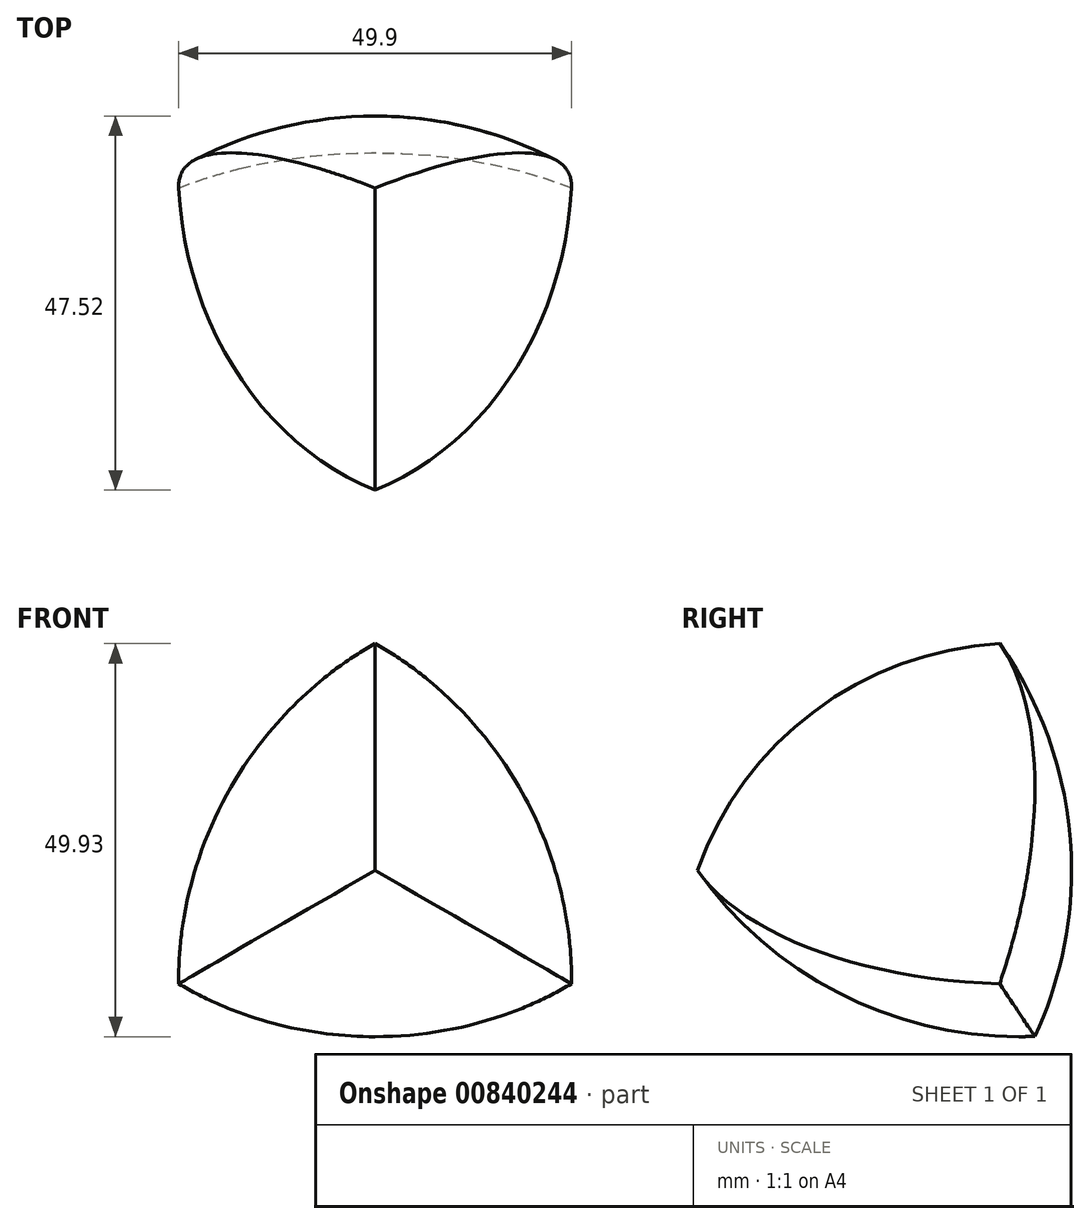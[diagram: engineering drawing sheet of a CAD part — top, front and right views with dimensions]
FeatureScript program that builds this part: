
annotation { "Feature Type Name" : "Feature", "Feature Type Description" : "" }
export const myFeature = defineFeature(function(context is Context, id is Id, definition is map)
    precondition{}
    {
        {
            var Q0;
            Q0=qCreatedBy(makeId("Front.planeOp"),FACE);
            var sketch = newSketch(context, id + "F0", { "sketchPlane" : qUnion([Q0])});
            skCircle(sketch, "E0", {"center": v(0, 0) * mm, "radius": 28.87 * mm, "construction": true});
            skCircle(sketch, "E1", {"center": v(0, 28.87) * mm, "radius": 50 * mm, "construction": true});
            skCircle(sketch, "E2", {"center": v(-25, -14.43) * mm, "radius": 50 * mm, "construction": true});
            skCircle(sketch, "E3", {"center": v(25, -14.43) * mm, "radius": 50 * mm, "construction": true});
            skSolve(sketch);
        }
        {
            var Q0;
            Q0=qCreatedBy(makeId("Front.planeOp"),FACE);
            var sketch = newSketch(context, id + "F1", { "sketchPlane" : qUnion([Q0])});
            skLineSegment(sketch, "E4", {"start": v(0, 0) * mm, "end": v(0, 85.02) * mm, "construction": true});
            skArc(sketch, "E5", {"start": v(0, -21.13) * mm, "mid": v(50, 28.87) * mm, "end": v(0, 78.87) * mm});
            skLineSegment(sketch, "E6", {"start": v(0, -21.13) * mm, "end": v(0, 78.87) * mm});
            skSolve(sketch);
        }
        {
            var Q0;
            Q0 = qSketchRegion(id + "F1", true);
            var Q1;
            Q1=sQuery(id+"F1.wireOp",EDGE,"E4");
            revolve(context, id + "F2", {"surfaceOperationType" : NewSurfaceOperationType.NEW, "entities" : qUnion([Q0]), "axis" : qUnion([Q1]), "revolveType" : RevolveType.FULL});
        }
        {
            var Q0;
            Q0=qCreatedBy(makeId("Front.planeOp"),FACE);
            var sketch = newSketch(context, id + "F3", { "sketchPlane" : qUnion([Q0])});
            skLineSegment(sketch, "E7", {"start": v(0, 0) * mm, "end": v(-97.44, -56.26) * mm, "construction": true});
            skLineSegment(sketch, "E8", {"start": v(0, 0) * mm, "end": v(-109.46, 0) * mm, "construction": true});
            skArc(sketch, "E9", {"start": v(-68.3, -39.43) * mm, "mid": v(0, -57.74) * mm, "end": v(18.3, 10.57) * mm});
            skLineSegment(sketch, "E10", {"start": v(-68.3, -39.43) * mm, "end": v(18.3, 10.57) * mm});
            skSolve(sketch);
        }
        {
            var Q0;
            Q0 = qSketchRegion(id + "F3", true);
            var Q1;
            Q1=sQuery(id+"F3.wireOp",EDGE,"E7");
            revolve(context, id + "F4", {"surfaceOperationType" : NewSurfaceOperationType.NEW, "entities" : qUnion([Q0]), "axis" : qUnion([Q1]), "revolveType" : RevolveType.FULL});
        }
        {
            var Q0;
            Q0=qCreatedBy(makeId("Front.planeOp"),FACE);
            var sketch = newSketch(context, id + "F5", { "sketchPlane" : qUnion([Q0])});
            skArc(sketch, "E11", {"start": v(-18.3, 10.57) * mm, "mid": v(0, -57.74) * mm, "end": v(68.3, -39.43) * mm});
            skLineSegment(sketch, "E12", {"start": v(0, 0) * mm, "end": v(97.2, -56.12) * mm, "construction": true});
            skLineSegment(sketch, "E13", {"start": v(-18.3, 10.57) * mm, "end": v(68.3, -39.43) * mm});
            skSolve(sketch);
        }
        {
            var Q0;
            Q0 = qSketchRegion(id + "F5", true);
            var Q1;
            Q1=sQuery(id+"F5.wireOp",EDGE,"E12");
            revolve(context, id + "F6", {"surfaceOperationType" : NewSurfaceOperationType.NEW, "entities" : qUnion([Q0]), "axis" : qUnion([Q1]), "revolveType" : RevolveType.FULL});
        }
        {
            var Q0;
            Q0=qCreatedBy(makeId("Top.planeOp"),FACE);
            var Q1;
            Q1=sQuery(id+"F0.wireOp",VERTEX,"E3.center");
            cPlane(context, id + "F7", {"entities" : qUnion([Q0, Q1]), "cplaneType" : CPlaneType.PLANE_POINT, "offset" : 25 * mm, "width" : 150 * mm, "height" : 150 * mm});
        }
        {
            var Q0;
            Q0=qCreatedBy(id+"F7.planeOp",FACE);
            var sketch = newSketch(context, id + "F8", { "sketchPlane" : qUnion([Q0])});
            skCircle(sketch, "E14", {"center": v(25, 0) * mm, "radius": 50 * mm, "construction": true});
            skCircle(sketch, "E15", {"center": v(-25, 0) * mm, "radius": 50 * mm, "construction": true});
            skSolve(sketch);
        }
        {
            var Q0;
            Q0=qCreatedBy(makeId("Top.planeOp"),FACE);
            var sketch = newSketch(context, id + "F9", { "sketchPlane" : qUnion([Q0])});
            skArc(sketch, "E16", {"start": v(0, 6.7) * mm, "mid": v(-50, -43.3) * mm, "end": v(0, -93.3) * mm});
            skLineSegment(sketch, "E17", {"start": v(0, 0) * mm, "end": v(0, -109.96) * mm, "construction": true});
            skLineSegment(sketch, "E18", {"start": v(0, 6.7) * mm, "end": v(0, -93.3) * mm});
            skSolve(sketch);
        }
        {
            var Q0;
            Q0 = qSketchRegion(id + "F9", true);
            var Q1;
            Q1=sQuery(id+"F9.wireOp",EDGE,"E17");
            revolve(context, id + "F10", {"surfaceOperationType" : NewSurfaceOperationType.NEW, "entities" : qUnion([Q0]), "axis" : qUnion([Q1]), "revolveType" : RevolveType.FULL});
        }
        {
            var Q0;
            Q0=makeQuery(id+"F2.opRevolve","SWEPT_BODY",BODY,{"disambiguationData":[OSD([sQuery(id+"F1.wireOp",EDGE,"E5"),sQuery(id+"F1.wireOp",EDGE,"E6")])]});
            var Q1;
            Q1=makeQuery(id+"F4.opRevolve","SWEPT_BODY",BODY,{"disambiguationData":[OSD([sQuery(id+"F3.wireOp",EDGE,"E9"),sQuery(id+"F3.wireOp",EDGE,"E10")])]});
            var Q2;
            Q2=makeQuery(id+"F6.opRevolve","SWEPT_BODY",BODY,{"disambiguationData":[OSD([sQuery(id+"F5.wireOp",EDGE,"E11"),sQuery(id+"F5.wireOp",EDGE,"E13")])]});
            var Q3;
            Q3=makeQuery(id+"F10.opRevolve","SWEPT_BODY",BODY,{"disambiguationData":[OSD([sQuery(id+"F9.wireOp",EDGE,"E16"),sQuery(id+"F9.wireOp",EDGE,"E18")])]});
            booleanBodies(context, id + "F11", {"operationType" : BooleanOperationType.INTERSECTION, "tools" : qUnion([Q0, Q1, Q2, Q3])});
        }
    });
